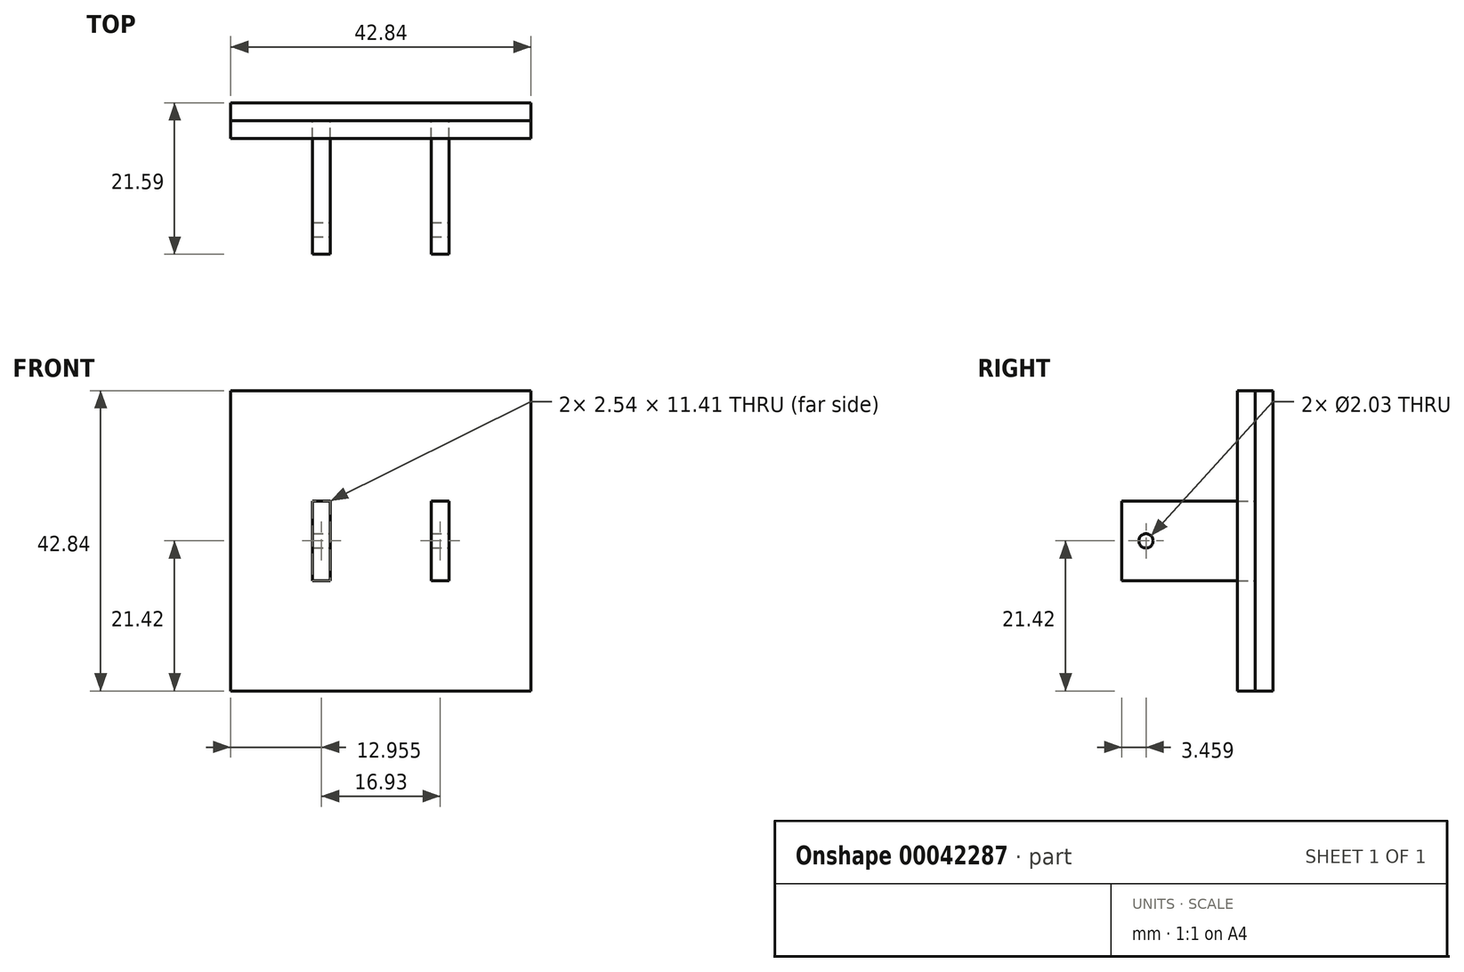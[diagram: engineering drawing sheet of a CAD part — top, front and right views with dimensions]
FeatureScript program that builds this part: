
annotation { "Feature Type Name" : "Feature", "Feature Type Description" : "" }
export const myFeature = defineFeature(function(context is Context, id is Id, definition is map)
    precondition{}
    {
        {
            var Q0;
            Q0=qCreatedBy(makeId("Front.planeOp"),FACE);
            var sketch = newSketch(context, id + "F0", { "sketchPlane" : qUnion([Q0])});
            skLineSegment(sketch, "E0.bottom", {"start": v(-21.42, 21.42) * mm, "end": v(21.42, 21.42) * mm});
            skLineSegment(sketch, "E0.top", {"start": v(-21.42, -21.42) * mm, "end": v(21.42, -21.42) * mm});
            skLineSegment(sketch, "E0.left", {"start": v(-21.42, 21.42) * mm, "end": v(-21.42, -21.42) * mm});
            skLineSegment(sketch, "E0.right", {"start": v(21.42, 21.42) * mm, "end": v(21.42, -21.42) * mm});
            skLineSegment(sketch, "E1", {"start": v(-21.42, 21.42) * mm, "end": v(21.42, -21.42) * mm, "construction": true});
            skSolve(sketch);
        }
        {
            var Q0;
            Q0 = qSketchRegion(id + "F0", true);
            extrude(context, id + "F1", {"entities" : qUnion([Q0]), "depth" : 2.54 * mm});
        }
        {
            var Q0;
            Q0=makeQuery(id+"F1.opExtrude","CAP_FACE",FACE,{"disambiguationData":[OSD([sQuery(id+"F0.wireOp",EDGE,"E0.bottom"),sQuery(id+"F0.wireOp",EDGE,"E0.top"),sQuery(id+"F0.wireOp",EDGE,"E0.left"),sQuery(id+"F0.wireOp",EDGE,"E0.right")])],"isStart":false});
            var sketch = newSketch(context, id + "F2", { "sketchPlane" : qUnion([Q0])});
            skLineSegment(sketch, "E2.bottom", {"start": v(-9.74, 5.7) * mm, "end": v(-7.2, 5.7) * mm});
            skLineSegment(sketch, "E2.top", {"start": v(-9.74, -5.7) * mm, "end": v(-7.2, -5.7) * mm});
            skLineSegment(sketch, "E2.left", {"start": v(-9.74, 5.7) * mm, "end": v(-9.74, -5.7) * mm});
            skLineSegment(sketch, "E2.right", {"start": v(-7.2, 5.7) * mm, "end": v(-7.2, -5.7) * mm});
            skLineSegment(sketch, "E3", {"start": v(0, 21.42) * mm, "end": v(0, -21.42) * mm, "construction": true});
            skLineSegment(sketch, "E4", {"start": v(-21.42, 0) * mm, "end": v(21.42, 0) * mm, "construction": true});
            skLineSegment(sketch, "E5.MirrorCS", {"start": v(7.2, 5.7) * mm, "end": v(7.2, -5.7) * mm});
            skLineSegment(sketch, "E6.MirrorCS", {"start": v(9.74, 5.7) * mm, "end": v(9.74, -5.7) * mm});
            skLineSegment(sketch, "E7.MirrorCS", {"start": v(9.74, -5.7) * mm, "end": v(7.2, -5.7) * mm});
            skLineSegment(sketch, "E8.MirrorCS", {"start": v(9.74, 5.7) * mm, "end": v(7.2, 5.7) * mm});
            skSolve(sketch);
        }
        {
            var Q0;
            Q0 = qSketchRegion(id + "F2", true);
            extrude(context, id + "F3", {"entities" : qUnion([Q0]), "operationType" : NewBodyOperationType.ADD, "depth" : 19.05 * mm});
        }
        {
            var Q0;
            Q0=makeQuery(id+"F3.opExtrude","SWEPT_FACE",FACE,{"disambiguationData":[OSD([sQuery(id+"F2.wireOp",EDGE,"E6.MirrorCS")])]});
            var sketch = newSketch(context, id + "F4", { "sketchPlane" : qUnion([Q0])});
            skCircle(sketch, "E9", {"center": v(-18.13, 0) * mm, "radius": 1.02 * mm});
            skSolve(sketch);
        }
        {
            var Q0;
            Q0=makeQuery(id+"F4.imprint","IMPRINT",FACE,{"disambiguationData":[TD([[makeQuery(id+"F4.imprint","IMPRINT",EDGE,{"derivedFrom":sQuery(id+"F4.wireOp",EDGE,"E9")}),1.0]])]});
            var Q1;
            Q1=sQuery(id+"F4.wireOp",EDGE,"E9");
            extrude(context, id + "F5", {"entities" : qUnion([Q0]), "operationType" : NewBodyOperationType.REMOVE, "surfaceEntities" : qUnion([Q1]), "endBound" : BoundingType.THROUGH_ALL, "oppositeDirection" : true, "depth" : 25.4 * mm});
        }
        {
            var Q0;
            Q0=makeQuery(id+"F1.opExtrude","CAP_FACE",FACE,{"disambiguationData":[OSD([sQuery(id+"F0.wireOp",EDGE,"E0.bottom"),sQuery(id+"F0.wireOp",EDGE,"E0.top"),sQuery(id+"F0.wireOp",EDGE,"E0.left"),sQuery(id+"F0.wireOp",EDGE,"E0.right")])],"isStart":false});
            extrude(context, id + "F6", {"entities" : qUnion([Q0]), "depth" : 2.54 * mm});
        }
    });
